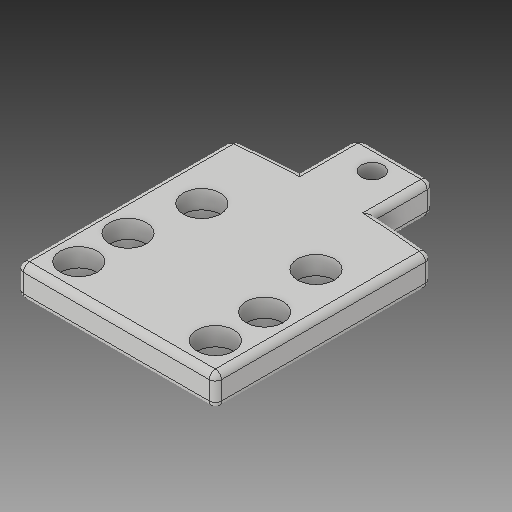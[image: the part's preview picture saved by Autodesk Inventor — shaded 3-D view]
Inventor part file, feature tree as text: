
AUTODESK INVENTOR PART (.ipt)
format: ipt  version: 2018 (Build 220112000, 112)  size: 290,304 bytes
history: native  units: mm
features: extrude x4, sketch x4, fillet x3, other x3, projected_geometry x1, reference x1
ambient origin geometry x8: Origin, YZ Plane, XZ Plane, XY Plane, X Axis, Y Axis, Z Axis, Center Point
bodies: Solid1 (feature_tree)
feature tree (16):
  extrude  "Extrusion1"  Depth=15.24mm TaperAngle=0.0deg
  extrude  "Extrusion2"  Depth=0.25mm
  extrude  "Extrusion6"  Depth=10.0mm
  extrude  "Extrusion7"  Depth=1.0mm
  fillet  "Fillet3"  Radius=5.0mm
  fillet  "Fillet4"  Radius=2.5mm
  fillet  "Fillet5"  Radius=8.0mm
  sketch  "Sketch1"  dims[d0=5.0038mm d1=0.0mm d2=15.24mm d3=0.0mm]
  sketch  "Sketch2"  dims[d4=0.25mm d5=0.25mm]
  projected_geometry  "Projected Loop1"
  sketch  "Sketch6"  dims[d23=10.0mm d24=10.0mm]
  reference  "Reference1"
  sketch  "Sketch7"  dims[d25=20.0mm d26=5.0mm d27=5.0mm d28=2.5mm d29=8.0mm d30=5.0mm d31=2.5mm d32=10.0mm d33=0.0mm d34=6.0mm d35=6.0mm d36=6.0mm d37=6.0mm d38=6.0mm d39=6.0mm d40=3.0mm d41=0.0mm d42=1.0mm d43=1.0mm d44=1.0mm]
  other  "<userpath>\OneDrive\Documents\Inventor\TSA\2018\Animatronics\Tortoise\TurtleAssembly.iam"
  other  "TurtleAssembly.iam"
  other  "Frame - Copy:1"
